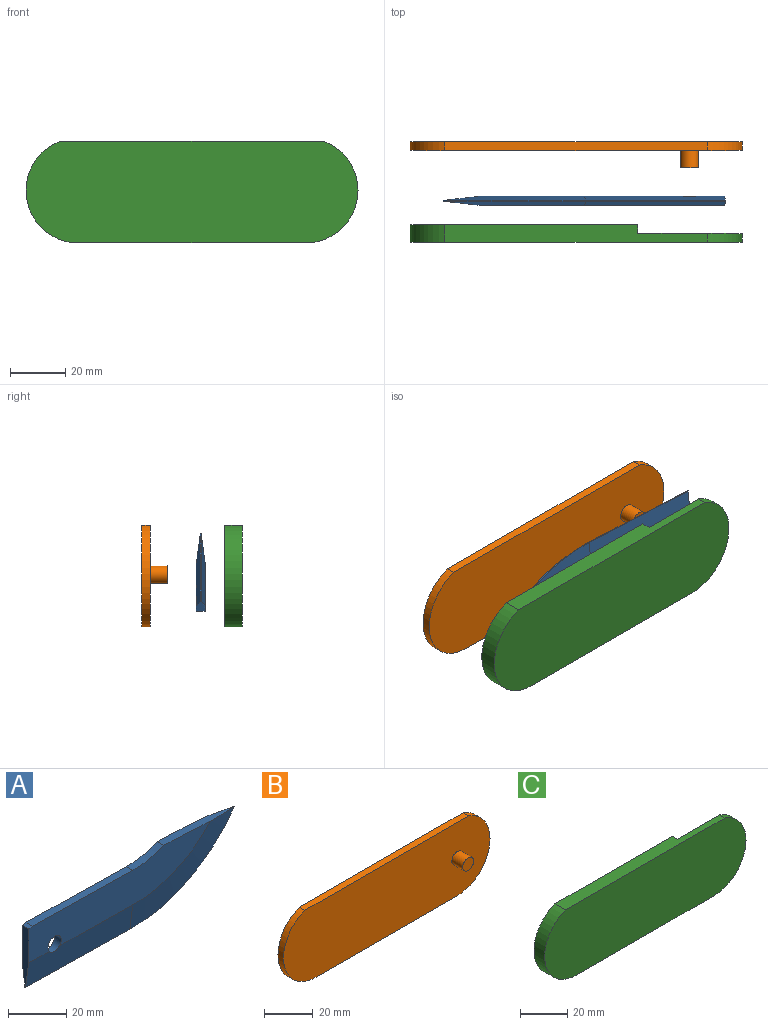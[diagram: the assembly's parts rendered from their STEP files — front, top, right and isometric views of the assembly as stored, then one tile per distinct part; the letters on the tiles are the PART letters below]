
ASSEMBLY  parts=3 mates=2
PART A: 14 faces, bbox 102.5x7x41.8 mm
  f0: bspline ~51.68x41.76mm, area 567.7mm2, adj f1,f5,f7,f8
  f1: plane 50.79x11.9mm, normal (0,0.99,-0.13), area 559.3mm2, adj f0,f2,f5,f6,f9
  f2: plane 25.4x3.18mm, normal (-1,0,0), area 64.7mm2, adj f1,f3,f4,f5,f6,f12
  f3: cylinder r=508mm len=3.18mm, axis (0,1,0), area 6.1mm2, adj f2,f4,f5,f11
  f4: plane 88.55x17.61mm, normal (0,-1,0), area 1150.7mm2, adj f2,f3,f8,f9,f10,f11,f12,f13
  f5: plane 88.55x17.61mm, normal (0,1,0), area 1150.7mm2, adj f0,f1,f2,f3,f8,f9,f10,f11
  f6: plane 50.79x0.89mm, normal (-0.02,0,-1), area 14mm2, adj f1,f2,f7,f12
  f7: cylinder r=60.22mm len=50.81mm, axis (0,1,0), area 16.5mm2, adj f0,f6,f8,f13
  f8: cylinder r=508mm len=35.66mm, axis (0,1,0), area 94.5mm2, adj f0,f4,f5,f7,f10,f13
  f9: cylinder r=3.21mm len=6.43mm, axis (0,1,0), area 62.7mm2, adj f1,f4,f5,f12
  f10: cylinder r=34.61mm len=15.15mm, axis (0,-1,0), area 49.4mm2, adj f4,f5,f8,f11
  f11: plane 48.88x3.18mm, normal (0.02,0,1), area 155.2mm2, adj f3,f4,f5,f10
  f12: plane 50.79x11.9mm, normal (0,-0.99,-0.13), area 559.3mm2, adj f2,f4,f6,f9,f13
  f13: bspline ~51.68x41.76mm, area 567.7mm2, adj f4,f7,f8,f12
PART B: 8 faces, bbox 120.3x9.5x37 mm
  f0: plane 95.25x3.18mm, normal (0,0,1), area 302.4mm2, adj f1,f3,f4,f5
  f1: cylinder r=19.05mm len=36.95mm, axis (0,1,0), area 168.9mm2, adj f0,f2,f4,f5
  f2: plane 82.22x3.18mm, normal (0,0,-1), area 261mm2, adj f1,f3,f4,f5
  f3: cylinder r=19.05mm len=36.95mm, axis (0,1,0), area 168.9mm2, adj f0,f2,f4,f5
  f4: plane 120.32x36.95mm, normal (0,-1,0), area 4136.5mm2, adj f0,f1,f2,f3,f6
  f5: plane 120.32x36.95mm, normal (0,1,0), area 4168.1mm2, adj f0,f1,f2,f3
  f6: cylinder r=3.17mm len=6.35mm, axis (0,1,0), area 126.7mm2, adj f4,f7
  f7: plane 6.35x6.35mm, normal (0,-1,0), area 31.7mm2, adj f6
PART C: 8 faces, bbox 120.3x6.4x37 mm
  f0: plane 37.77x36.95mm, normal (0,1,0), area 1256.7mm2, adj f1,f3,f4,f6
  f1: plane 95.25x6.35mm, normal (0,0,1), area 524.7mm2, adj f0,f2,f4,f5,f6,f7
  f2: cylinder r=19.05mm len=36.95mm, axis (0,1,0), area 337.8mm2, adj f1,f3,f5,f7
  f3: plane 82.22x6.35mm, normal (0,0,-1), area 462.7mm2, adj f0,f2,f4,f5,f6,f7
  f4: cylinder r=19.05mm len=36.95mm, axis (0,1,0), area 168.9mm2, adj f0,f1,f3,f5
  f5: plane 120.32x36.95mm, normal (0,-1,0), area 4168.1mm2, adj f1,f2,f3,f4
  f6: plane 36.95x3.18mm, normal (1,0,0), area 117.3mm2, adj f0,f1,f3,f7
  f7: plane 82.55x36.95mm, normal (0,1,0), area 2911.4mm2, adj f1,f2,f3,f6
PLACE A rot(axis=(0,-1,0),178.2deg) t=(128.8,-43.82,-22.01)mm
PLACE B t=(87.69,-24,-22.01)mm
PLACE C t=(87.69,-57.3,-22.01)mm
MATE cylindrical B.f1 <-> C.f2  axis (0,-1,0) through (46.58,-27.18,-22.01)mm
MATE cylindrical B.f3 <-> A.f9  axis (0,-1,0) through (128.8,-33.53,-22.01)mm
